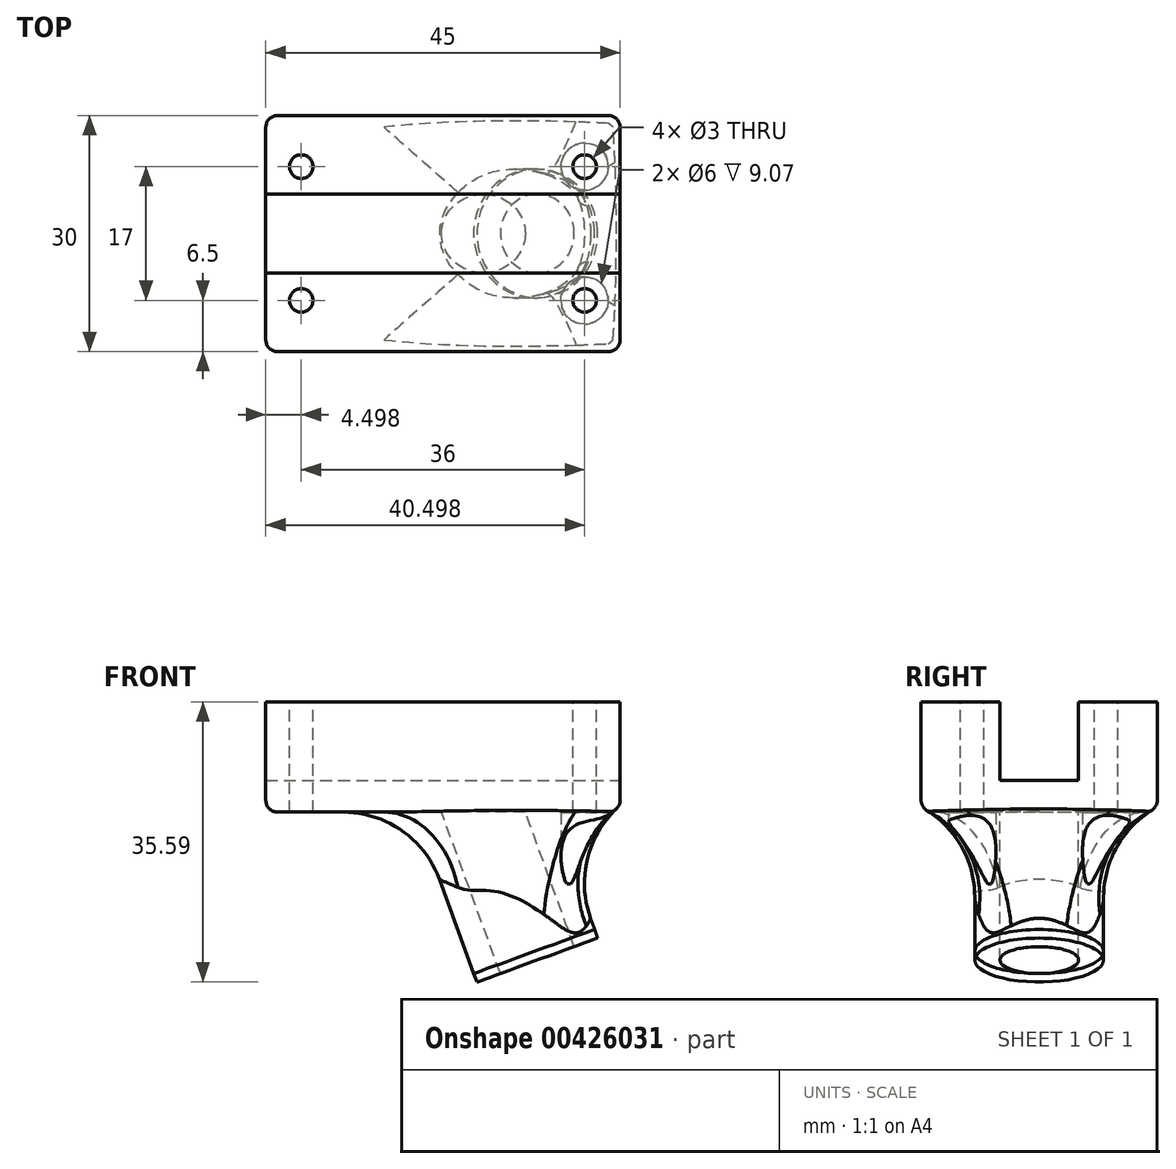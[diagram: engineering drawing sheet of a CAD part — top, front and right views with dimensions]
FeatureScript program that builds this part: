
annotation { "Feature Type Name" : "Feature", "Feature Type Description" : "" }
export const myFeature = defineFeature(function(context is Context, id is Id, definition is map)
    precondition{}
    {
        {
            var Q0;
            Q0=qCreatedBy(makeId("Front.planeOp"),FACE);
            var sketch = newSketch(context, id + "F0", { "sketchPlane" : qUnion([Q0])});
            skLineSegment(sketch, "E0", {"start": v(-9.37, 25.74) * mm, "end": v(0, 0) * mm});
            skLineSegment(sketch, "E1", {"start": v(-3.39, 0) * mm, "end": v(-12.36, 24.65) * mm});
            skLineSegment(sketch, "E2", {"start": v(-10.87, 44.48) * mm, "end": v(5.32, 0) * mm, "construction": true});
            skLineSegment(sketch, "E3", {"start": v(-9.37, 25.74) * mm, "end": v(-12.36, 24.65) * mm});
            skLineSegment(sketch, "E4", {"start": v(0, 0) * mm, "end": v(-2.97, -1.08) * mm});
            skLineSegment(sketch, "E5", {"start": v(-2.97, -1.08) * mm, "end": v(-3.39, 0) * mm});
            skPoint(sketch, "E6.orphan", {"position": v(-12.75, 25.74) * mm});
            skSolve(sketch);
        }
        {
            var Q0;
            Q0=makeQuery(id+"F0.imprint","IMPRINT",FACE,{"disambiguationData":[TD([[makeQuery(id+"F0.imprint","IMPRINT",EDGE,{"derivedFrom":sQuery(id+"F0.wireOp",EDGE,"E0")}),-1.0]])]});
            var Q1;
            Q1=sQuery(id+"F0.wireOp",EDGE,"E2");
            revolve(context, id + "F1", {"surfaceOperationType" : NewSurfaceOperationType.NEW, "entities" : qUnion([Q0]), "axis" : qUnion([Q1]), "revolveType" : RevolveType.FULL});
        }
        {
            var Q0;
            Q0=qCreatedBy(makeId("Front.planeOp"),FACE);
            var sketch = newSketch(context, id + "F2", { "sketchPlane" : qUnion([Q0])});
            skLineSegment(sketch, "E7.bottom", {"start": v(15.22, 20.5) * mm, "end": v(-29.78, 20.5) * mm});
            skLineSegment(sketch, "E7.top", {"start": v(15.22, 38.5) * mm, "end": v(-29.78, 38.5) * mm});
            skLineSegment(sketch, "E7.left", {"start": v(15.22, 20.5) * mm, "end": v(15.22, 38.5) * mm});
            skLineSegment(sketch, "E7.right", {"start": v(-29.78, 20.5) * mm, "end": v(-29.78, 38.5) * mm});
            skSolve(sketch);
        }
        {
            var Q0;
            Q0=makeQuery(id+"F2.imprint","IMPRINT",FACE,{"disambiguationData":[TD([[makeQuery(id+"F2.imprint","IMPRINT",EDGE,{"derivedFrom":sQuery(id+"F2.wireOp",EDGE,"E7.bottom")}),-1.0]])]});
            extrude(context, id + "F3", {"entities" : qUnion([Q0]), "operationType" : NewBodyOperationType.ADD, "depth" : 15 * mm, "offsetDistance" : 25 * mm});
        }
        {
            var Q0;
            Q0 = qSketchRegion(id + "F2", true);
            extrude(context, id + "F4", {"entities" : qUnion([Q0]), "operationType" : NewBodyOperationType.ADD, "oppositeDirection" : true, "depth" : 15 * mm, "offsetDistance" : 25 * mm});
        }
        {
            var Q0;
            {var subQ0=sQuery(id+"F2.wireOp",EDGE,"E7.left");Q0=makeQuery(id+"F4.boolean.opBoolean","MERGE",FACE,{"derivedFrom":[makeQuery(id+"F3.opExtrude","SWEPT_FACE",FACE,{"disambiguationData":[OSD([subQ0])]}),makeQuery(id+"F4.opExtrude","SWEPT_FACE",FACE,{"disambiguationData":[OSD([subQ0])]})]});}
            var sketch = newSketch(context, id + "F5", { "sketchPlane" : qUnion([Q0])});
            skLineSegment(sketch, "E8", {"start": v(-15, 29.5) * mm, "end": v(15, 29.5) * mm, "construction": true});
            skLineSegment(sketch, "E9.bottom", {"start": v(5, 24.5) * mm, "end": v(-5, 24.5) * mm});
            skLineSegment(sketch, "E9.top", {"start": v(5, 34.5) * mm, "end": v(-5, 34.5) * mm});
            skLineSegment(sketch, "E9.left", {"start": v(5, 24.5) * mm, "end": v(5, 34.5) * mm});
            skLineSegment(sketch, "E9.right", {"start": v(-5, 24.5) * mm, "end": v(-5, 34.5) * mm});
            skPoint(sketch, "E9.middle", {"position": v(0, 29.5) * mm});
            skSolve(sketch);
        }
        {
            var Q0;
            Q0 = qSketchRegion(id + "F5", true);
            extrude(context, id + "F6", {"entities" : qUnion([Q0]), "operationType" : NewBodyOperationType.REMOVE, "oppositeDirection" : true, "depth" : 45 * mm, "offsetDistance" : 25 * mm});
        }
        {
            var Q0;
            {var subQ0=sQuery(id+"F2.wireOp",EDGE,"E7.right");var subQ1=sQuery(id+"F2.wireOp",EDGE,"E7.top");Q0=makeQuery(id+"F4.boolean.opBoolean","MERGE",EDGE,{"derivedFrom":[makeQuery(id+"F3.opExtrude","SWEPT_EDGE",EDGE,{"disambiguationData":[OSD([subQ1,subQ0])]}),makeQuery(id+"F4.opExtrude","SWEPT_EDGE",EDGE,{"disambiguationData":[OSD([subQ1,subQ0])]})]});}
            var Q1;
            Q1=makeQuery(id+"F4.opExtrude","CAP_EDGE",EDGE,{"disambiguationData":[OSD([sQuery(id+"F2.wireOp",EDGE,"E7.right")])],"isStart":false});
            var Q2;
            {var subQ0=sQuery(id+"F2.wireOp",EDGE,"E7.right");var subQ1=sQuery(id+"F2.wireOp",EDGE,"E7.bottom");Q2=makeQuery(id+"F4.boolean.opBoolean","MERGE",EDGE,{"derivedFrom":[makeQuery(id+"F3.opExtrude","SWEPT_EDGE",EDGE,{"disambiguationData":[OSD([subQ1,subQ0])]}),makeQuery(id+"F4.opExtrude","SWEPT_EDGE",EDGE,{"disambiguationData":[OSD([subQ1,subQ0])]})]});}
            var Q3;
            Q3=makeQuery(id+"F3.opExtrude","CAP_EDGE",EDGE,{"disambiguationData":[OSD([sQuery(id+"F2.wireOp",EDGE,"E7.right")])],"isStart":false});
            var Q4;
            Q4=makeQuery(id+"F3.opExtrude","CAP_EDGE",EDGE,{"disambiguationData":[OSD([sQuery(id+"F2.wireOp",EDGE,"E7.top")])],"isStart":false});
            var Q5;
            Q5=makeQuery(id+"F4.opExtrude","CAP_EDGE",EDGE,{"disambiguationData":[OSD([sQuery(id+"F2.wireOp",EDGE,"E7.top")])],"isStart":false});
            var Q6;
            {var subQ0=sQuery(id+"F2.wireOp",EDGE,"E7.left");var subQ1=sQuery(id+"F2.wireOp",EDGE,"E7.top");Q6=makeQuery(id+"F4.boolean.opBoolean","MERGE",EDGE,{"derivedFrom":[makeQuery(id+"F3.opExtrude","SWEPT_EDGE",EDGE,{"disambiguationData":[OSD([subQ1,subQ0])]}),makeQuery(id+"F4.opExtrude","SWEPT_EDGE",EDGE,{"disambiguationData":[OSD([subQ1,subQ0])]})]});}
            var Q7;
            Q7=makeQuery(id+"F3.opExtrude","CAP_EDGE",EDGE,{"disambiguationData":[OSD([sQuery(id+"F2.wireOp",EDGE,"E7.left")])],"isStart":false});
            var Q8;
            Q8=makeQuery(id+"F4.opExtrude","CAP_EDGE",EDGE,{"disambiguationData":[OSD([sQuery(id+"F2.wireOp",EDGE,"E7.left")])],"isStart":false});
            var Q9;
            Q9=makeQuery(id+"F3.opExtrude","CAP_EDGE",EDGE,{"disambiguationData":[OSD([sQuery(id+"F2.wireOp",EDGE,"E7.bottom")])],"isStart":false});
            var Q10;
            Q10=makeQuery(id+"F4.opExtrude","CAP_EDGE",EDGE,{"disambiguationData":[OSD([sQuery(id+"F2.wireOp",EDGE,"E7.bottom")])],"isStart":false});
            var Q11;
            {var subQ0=sQuery(id+"F2.wireOp",EDGE,"E7.left");var subQ1=sQuery(id+"F2.wireOp",EDGE,"E7.bottom");Q11=makeQuery(id+"F4.boolean.opBoolean","MERGE",EDGE,{"derivedFrom":[makeQuery(id+"F3.opExtrude","SWEPT_EDGE",EDGE,{"disambiguationData":[OSD([subQ1,subQ0])]}),makeQuery(id+"F4.opExtrude","SWEPT_EDGE",EDGE,{"disambiguationData":[OSD([subQ1,subQ0])]})]});}
            fillet(context, id + "F7", {"entities" : qUnion([Q0, Q1, Q2, Q3, Q4, Q5, Q6, Q7, Q8, Q9, Q10, Q11]), "radius" : 1.5 * mm, "tangentPropagation" : true, "allowEdgeOverflow" : false});
        }
        {
            var Q0;
            Q0=makeQuery(id+"F4.boolean.opBoolean","INTERSECT",EDGE,{"derivedFrom":[makeQuery(id+"F1.opRevolve","SWEPT_FACE",FACE,{"disambiguationData":[OSD([sQuery(id+"F0.wireOp",EDGE,"E1")])]}),makeQuery(id+"F4.opExtrude","SWEPT_FACE",FACE,{"disambiguationData":[OSD([sQuery(id+"F2.wireOp",EDGE,"E7.bottom")])]})]});
            fillet(context, id + "F8", {"entities" : qUnion([Q0]), "radius" : 13 * mm, "tangentPropagation" : true, "allowEdgeOverflow" : false});
        }
        {
            var Q0;
            {var subQ0=sQuery(id+"F2.wireOp",EDGE,"E7.left");Q0=makeQuery(id+"F4.boolean.opBoolean","MERGE",FACE,{"derivedFrom":[makeQuery(id+"F3.opExtrude","SWEPT_FACE",FACE,{"disambiguationData":[OSD([subQ0])]}),makeQuery(id+"F4.opExtrude","SWEPT_FACE",FACE,{"disambiguationData":[OSD([subQ0])]})]});}
            var sketch = newSketch(context, id + "F9", { "sketchPlane" : qUnion([Q0])});
            skLineSegment(sketch, "E10", {"start": v(-13.23, 34.5) * mm, "end": v(15.13, 34.5) * mm, "construction": true});
            skLineSegment(sketch, "E11.bottom", {"start": v(-17.95, 34.5) * mm, "end": v(20.41, 34.5) * mm});
            skLineSegment(sketch, "E11.top", {"start": v(-17.95, 41.21) * mm, "end": v(20.41, 41.21) * mm});
            skLineSegment(sketch, "E11.left", {"start": v(-17.95, 34.5) * mm, "end": v(-17.95, 41.21) * mm});
            skLineSegment(sketch, "E11.right", {"start": v(20.41, 34.5) * mm, "end": v(20.41, 41.21) * mm});
            skSolve(sketch);
        }
        {
            var Q0;
            Q0 = qSketchRegion(id + "F9", true);
            extrude(context, id + "F10", {"entities" : qUnion([Q0]), "operationType" : NewBodyOperationType.REMOVE, "oppositeDirection" : true, "depth" : 46.9 * mm, "offsetDistance" : 25 * mm});
        }
        {
            var Q0;
            Q0=makeQuery(id+"F10.boolean.opBoolean","COPY",FACE,{"disambiguationData":[TD([makeQuery(id+"F6.boolean.opBoolean","COPY",FACE,{"derivedFrom":makeQuery(id+"F6.opExtrude","SWEPT_FACE",FACE,{"disambiguationData":[OSD([sQuery(id+"F5.wireOp",EDGE,"E9.left")])]})})])],"derivedFrom":makeQuery(id+"F10.opExtrude","SWEPT_FACE",FACE,{"disambiguationData":[OSD([sQuery(id+"F9.wireOp",EDGE,"E11.bottom")])]})});
            var sketch = newSketch(context, id + "F11", { "sketchPlane" : qUnion([Q0])});
            skLineSegment(sketch, "E12", {"start": v(10.72, -15) * mm, "end": v(10.72, -2) * mm, "construction": true});
            skCircle(sketch, "E13", {"center": v(10.72, -8.5) * mm, "radius": 1.5 * mm});
            skLineSegment(sketch, "E14", {"start": v(15.22, 0) * mm, "end": v(-29.78, 0) * mm, "construction": true});
            skLineSegment(sketch, "E15", {"start": v(-7.28, -10.52) * mm, "end": v(-7.28, -10.27) * mm, "construction": true});
            skPoint(sketch, "E15.startSnap0", {"position": v(-7.28, 0) * mm});
            skPoint(sketch, "E15.endSnap0", {"position": v(-7.28, 15) * mm});
            skCircle(sketch, "E16.MirrorC", {"center": v(-25.28, -8.5) * mm, "radius": 1.5 * mm});
            skCircle(sketch, "E17.MirrorC", {"center": v(10.72, 8.5) * mm, "radius": 1.5 * mm});
            skCircle(sketch, "E18.MirrorC", {"center": v(-25.28, 8.5) * mm, "radius": 1.5 * mm});
            skSolve(sketch);
        }
        {
            var Q0;
            Q0 = qSketchRegion(id + "F11", true);
            extrude(context, id + "F12", {"entities" : qUnion([Q0]), "operationType" : NewBodyOperationType.REMOVE, "oppositeDirection" : true, "depth" : 16.7 * mm, "offsetDistance" : 25 * mm});
        }
        {
            var Q0;
            Q0=qCreatedBy(makeId("Top.planeOp"),FACE);
            cPlane(context, id + "F13", {"entities" : qUnion([Q0]), "cplaneType" : CPlaneType.OFFSET, "offset" : 11.4 * mm, "width" : 150 * mm, "height" : 150 * mm});
        }
        {
            var Q0;
            Q0=qCreatedBy(id+"F13.planeOp",FACE);
            var sketch = newSketch(context, id + "F14", { "sketchPlane" : qUnion([Q0])});
            skCircle(sketch, "E19.0", {"center": v(10.72, -8.5) * mm, "radius": 1.5 * mm, "construction": true});
            skCircle(sketch, "E19.1", {"center": v(10.72, 8.5) * mm, "radius": 1.5 * mm, "construction": true});
            skCircle(sketch, "E20", {"center": v(10.72, -8.5) * mm, "radius": 3 * mm});
            skCircle(sketch, "E21.MirrorC", {"center": v(10.72, 8.5) * mm, "radius": 3 * mm});
            skSolve(sketch);
        }
        {
            var Q0;
            Q0 = qSketchRegion(id + "F14", true);
            extrude(context, id + "F15", {"entities" : qUnion([Q0]), "operationType" : NewBodyOperationType.REMOVE, "depth" : 9.07 * mm, "offsetDistance" : 25 * mm});
        }
    });
